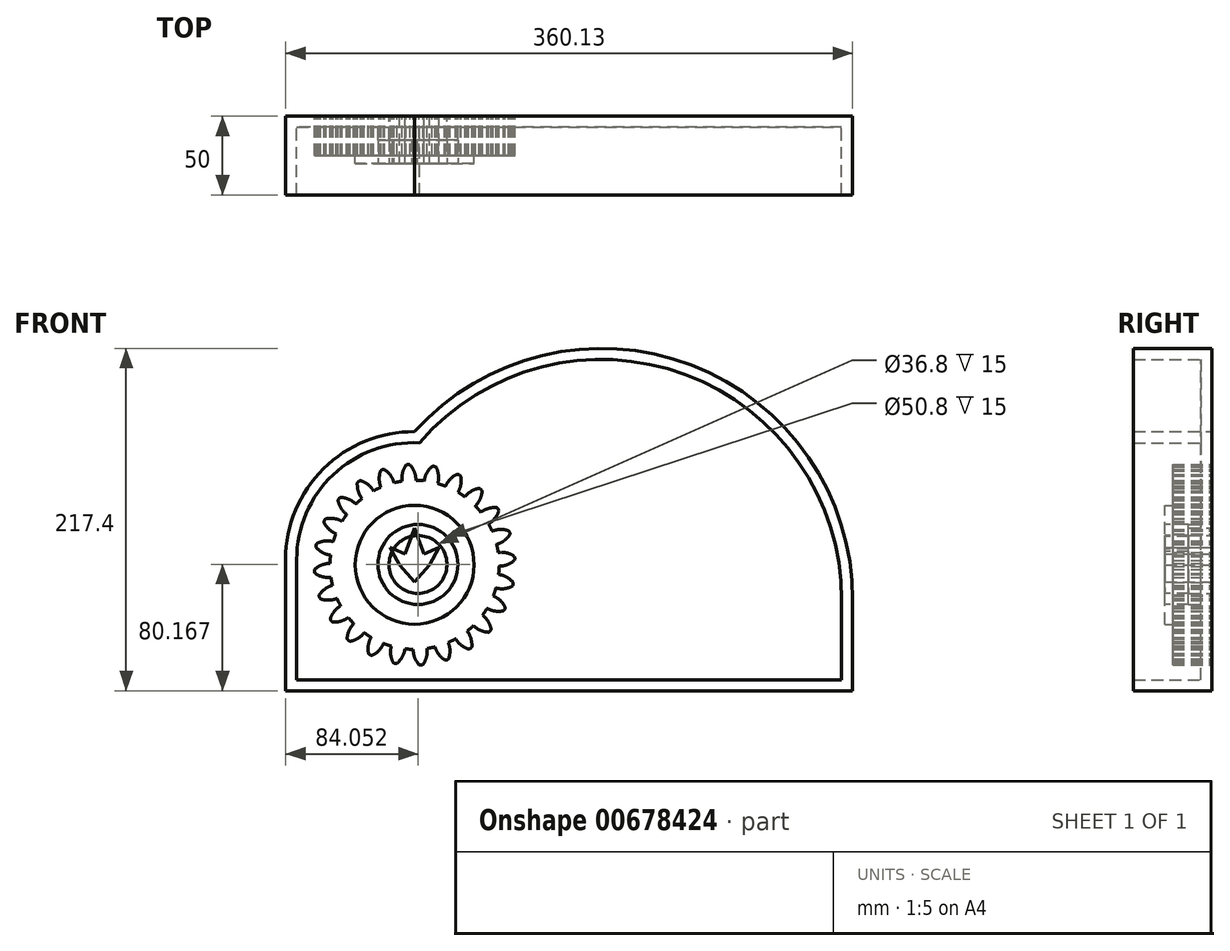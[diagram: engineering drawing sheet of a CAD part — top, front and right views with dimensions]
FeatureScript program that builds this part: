
annotation { "Feature Type Name" : "Feature", "Feature Type Description" : "" }
export const myFeature = defineFeature(function(context is Context, id is Id, definition is map)
    precondition{}
    {
        {
            var Q0;
            Q0=qCreatedBy(makeId("Front.planeOp"),FACE);
            var sketch = newSketch(context, id + "F0", { "sketchPlane" : qUnion([Q0])});
            skCircle(sketch, "E0", {"center": v(0, 0) * mm, "radius": 53.72 * mm});
            skCircle(sketch, "E1", {"center": v(0, 0) * mm, "radius": 58.67 * mm, "construction": true});
            skCircle(sketch, "E2", {"center": v(0, 0) * mm, "radius": 63.5 * mm, "construction": true});
            skLineSegment(sketch, "E3", {"start": v(0, 0) * mm, "end": v(0, 159.95) * mm, "construction": true});
            skLineSegment(sketch, "E4", {"start": v(0, 0) * mm, "end": v(-12.76, 194.75) * mm, "construction": true});
            skLineSegment(sketch, "E5", {"start": v(0, 58.67) * mm, "end": v(-65.03, 58.67) * mm, "construction": true});
            skLineSegment(sketch, "E6", {"start": v(0, 58.67) * mm, "end": v(-68.02, 33.92) * mm, "construction": true});
            skCircle(sketch, "E7", {"center": v(0, 0) * mm, "radius": 55.14 * mm, "construction": true});
            skCircle(sketch, "E8", {"center": v(0, 58.67) * mm, "radius": 14.6 * mm, "construction": true});
            skCircle(sketch, "E9", {"center": v(-13.72, 53.68) * mm, "radius": 14.6 * mm, "construction": true});
            skArc(sketch, "E10", {"start": v(0, 58.67) * mm, "mid": v(-1.2, 61.19) * mm, "end": v(-2.86, 63.44) * mm});
            skArc(sketch, "E11", {"start": v(0.88, 53.71) * mm, "mid": v(0.66, 56.23) * mm, "end": v(0, 58.67) * mm});
            skArc(sketch, "E12.MirrorCS", {"start": v(-7.66, 58.17) * mm, "mid": v(-6.8, 60.82) * mm, "end": v(-5.45, 63.27) * mm});
            skArc(sketch, "E13.MirrorCS", {"start": v(-7.88, 53.14) * mm, "mid": v(-8, 55.67) * mm, "end": v(-7.66, 58.17) * mm});
            skArc(sketch, "E14", {"start": v(-2.86, 63.44) * mm, "mid": v(-4.17, 63.67) * mm, "end": v(-5.45, 63.27) * mm});
            skCircle(sketch, "E15", {"center": v(0, 0) * mm, "radius": 37.75 * mm});
            skLineSegment(sketch, "E16", {"start": v(-9.63, 0) * mm, "end": v(-15.66, 11.07) * mm});
            skLineSegment(sketch, "E17", {"start": v(-15.66, 11.07) * mm, "end": v(-5.9, 6.75) * mm});
            skLineSegment(sketch, "E18", {"start": v(-5.9, 6.75) * mm, "end": v(0, 23.42) * mm});
            skLineSegment(sketch, "E19", {"start": v(-9.63, 0) * mm, "end": v(0, -10.78) * mm});
            skLineSegment(sketch, "E20.MirrorCS", {"start": v(5.9, 6.75) * mm, "end": v(0, 23.42) * mm});
            skLineSegment(sketch, "E21.MirrorCS", {"start": v(15.66, 11.07) * mm, "end": v(5.9, 6.75) * mm});
            skLineSegment(sketch, "E22.MirrorCS", {"start": v(9.63, 0) * mm, "end": v(15.66, 11.07) * mm});
            skLineSegment(sketch, "E23.MirrorCS", {"start": v(9.63, 0) * mm, "end": v(0, -10.78) * mm});
            skSolve(sketch);
        }
        {
            var Q0;
            Q0=makeQuery(id+"F0.imprint","IMPRINT",FACE,{"disambiguationData":[TD([[makeQuery(id+"F0.imprint","IMPRINT",EDGE,{"derivedFrom":sQuery(id+"F0.wireOp",EDGE,"E10")}),1.0]])]});
            var Q1;
            Q1=makeQuery(id+"F0.imprint","IMPRINT",FACE,{"disambiguationData":[TD([[makeQuery(id+"F0.imprint","IMPRINT",EDGE,{"derivedFrom":sQuery(id+"F0.wireOp",EDGE,"E15")}),-1.0]])]});
            extrude(context, id + "F1", {"entities" : qUnion([Q0, Q1]), "depth" : 25 * mm, "offsetDistance" : 25 * mm});
        }
        {
            var Q0;
            Q0=makeQuery(id+"F1.opExtrude","SWEPT_BODY",BODY,{"disambiguationData":[OSD([sQuery(id+"F0.wireOp",EDGE,"E0"),sQuery(id+"F0.wireOp",EDGE,"E10"),sQuery(id+"F0.wireOp",EDGE,"E11"),sQuery(id+"F0.wireOp",EDGE,"E12.MirrorCS"),sQuery(id+"F0.wireOp",EDGE,"E13.MirrorCS"),sQuery(id+"F0.wireOp",EDGE,"E14")])]});
            var Q1;
            Q1=makeQuery(id+"F1.opExtrude","SWEPT_FACE",FACE,{"disambiguationData":[OSD([sQuery(id+"F0.wireOp",EDGE,"E0")])]});
            circularPattern(context, id + "F2", {"entities" : qUnion([Q0]), "axis" : qUnion([Q1]), "angle" : 360 * degree, "instanceCount" : 24, "equalSpace" : true});
        }
        {
            var Q0;
            Q0=makeQuery(id+"F0.imprint","IMPRINT",FACE,{"disambiguationData":[TD([[makeQuery(id+"F0.imprint","IMPRINT",EDGE,{"derivedFrom":sQuery(id+"F0.wireOp",EDGE,"E15")}),1.0]])]});
            extrude(context, id + "F3", {"entities" : qUnion([Q0]), "operationType" : NewBodyOperationType.ADD, "depth" : 30 * mm, "offsetDistance" : 25 * mm});
        }
        {
            var Q0;
            Q0=qCreatedBy(makeId("Front.planeOp"),FACE);
            var sketch = newSketch(context, id + "F4", { "sketchPlane" : qUnion([Q0])});
            skLineSegment(sketch, "E24", {"start": v(-81.88, -79.95) * mm, "end": v(278.25, -79.95) * mm});
            skLineSegment(sketch, "E25", {"start": v(-81.88, -79.95) * mm, "end": v(-81.88, 3.47) * mm});
            skArc(sketch, "E26", {"start": v(0, 84.55) * mm, "mid": v(-57.85, 61.09) * mm, "end": v(-81.88, 3.47) * mm});
            skLineSegment(sketch, "E27", {"start": v(278.25, -79.95) * mm, "end": v(278.25, -22.12) * mm});
            skArc(sketch, "E28", {"start": v(278.25, -22.12) * mm, "mid": v(175.8, 126.88) * mm, "end": v(0, 84.55) * mm});
            skCircle(sketch, "E29", {"center": v(2.17, 0.22) * mm, "radius": 18.4 * mm});
            skSolve(sketch);
        }
        {
            var Q0;
            Q0=makeQuery(id+"F4.imprint","IMPRINT",FACE,{"disambiguationData":[TD([[makeQuery(id+"F4.imprint","IMPRINT",EDGE,{"derivedFrom":sQuery(id+"F4.wireOp",EDGE,"E24")}),1.0]])]});
            extrude(context, id + "F5", {"entities" : qUnion([Q0]), "depth" : 50 * mm, "offsetDistance" : 25 * mm});
        }
        {
            var Q0;
            Q0=makeQuery(id+"F5.opExtrude","CAP_FACE",FACE,{"disambiguationData":[OSD([sQuery(id+"F4.wireOp",EDGE,"E24"),sQuery(id+"F4.wireOp",EDGE,"E25"),sQuery(id+"F4.wireOp",EDGE,"E26"),sQuery(id+"F4.wireOp",EDGE,"E27"),sQuery(id+"F4.wireOp",EDGE,"E28"),sQuery(id+"F4.wireOp",EDGE,"12c102c6-9bed-4f41-a9be-72ba41c20a8b"),sQuery(id+"F4.wireOp",EDGE,"967591d2-516f-4b5f-87a6-769b8b4d6096"),sQuery(id+"F4.wireOp",EDGE,"845599f8-ed41-4376-9980-788dd2c9d39a"),sQuery(id+"F4.wireOp",EDGE,"5b5c5c54-f0c3-4110-8fe7-2e6e4a83caaf"),sQuery(id+"F4.wireOp",EDGE,"f937d9f3-1abb-48cb-b538-4b2e71d97948.MirrorCS"),sQuery(id+"F4.wireOp",EDGE,"473fbc50-4437-4217-a78b-21279ffe1702.MirrorCS"),sQuery(id+"F4.wireOp",EDGE,"4ad7e60a-657b-49df-9f1c-0dbd1bc47104.MirrorCS"),sQuery(id+"F4.wireOp",EDGE,"6fe29303-5492-4566-b12e-0e24b3beb40a.MirrorCS"),sQuery(id+"F4.wireOp",EDGE,"14d6fb4b-1910-4295-8ef4-05344891b2d8")])],"isStart":false});
            shell(context, id + "F6", {"entities" : qUnion([Q0]), "thickness" : 7 * mm});
        }
        {
            var Q0;
            {var subQ0=sQuery(id+"F4.wireOp",EDGE,"6fe29303-5492-4566-b12e-0e24b3beb40a.MirrorCS");var subQ1=sQuery(id+"F4.wireOp",EDGE,"4ad7e60a-657b-49df-9f1c-0dbd1bc47104.MirrorCS");var subQ2=sQuery(id+"F4.wireOp",EDGE,"473fbc50-4437-4217-a78b-21279ffe1702.MirrorCS");var subQ3=sQuery(id+"F4.wireOp",EDGE,"f937d9f3-1abb-48cb-b538-4b2e71d97948.MirrorCS");var subQ4=sQuery(id+"F4.wireOp",EDGE,"5b5c5c54-f0c3-4110-8fe7-2e6e4a83caaf");var subQ5=sQuery(id+"F4.wireOp",EDGE,"845599f8-ed41-4376-9980-788dd2c9d39a");var subQ6=sQuery(id+"F4.wireOp",EDGE,"967591d2-516f-4b5f-87a6-769b8b4d6096");var subQ7=sQuery(id+"F4.wireOp",EDGE,"12c102c6-9bed-4f41-a9be-72ba41c20a8b");var subQ8=sQuery(id+"F4.wireOp",EDGE,"E28");var subQ9=sQuery(id+"F4.wireOp",EDGE,"E27");var subQ10=sQuery(id+"F4.wireOp",EDGE,"E26");var subQ11=sQuery(id+"F4.wireOp",EDGE,"E25");var subQ12=sQuery(id+"F4.wireOp",EDGE,"E24");Q0=makeQuery(id+"F6.opShell","OFFSET_FACE",FACE,{"disambiguationData":[OSD([subQ12,subQ11,subQ10,subQ9,subQ8,subQ7,subQ6,subQ5,subQ4,subQ3,subQ2,subQ1,subQ0]),TDD([makeQuery(id+"F5.opExtrude","CAP_FACE",FACE,{"disambiguationData":[OSD([subQ12,subQ11,subQ10,subQ9,subQ8,subQ7,subQ6,subQ5,subQ4,subQ3,subQ2,subQ1,subQ0])],"isStart":false})])]});}
            extrude(context, id + "F7", {"entities" : qUnion([Q0]), "operationType" : NewBodyOperationType.REMOVE, "oppositeDirection" : true, "depth" : 35 * mm, "offsetDistance" : 25 * mm});
        }
    });
